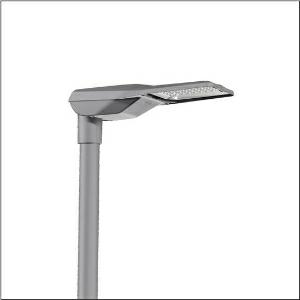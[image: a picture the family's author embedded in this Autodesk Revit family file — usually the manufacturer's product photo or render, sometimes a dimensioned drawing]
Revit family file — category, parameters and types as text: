
# Revit family: streetlight_sl_21_iq_mini___st1_0a_5xe2d31g08gb_f91a
name_source: partatom
category: Lighting Fixtures
units: mm (PartAtom-declared; Revit-internal decimal feet)

## family parameters
Cut with Voids When Loaded = No
Host = Face
Light Source = No
Part Type = Normal
Room Calculation Point = No
Round Connector Dimension = Use Diameter
Shared = No

## types (1)
- --- (1 x LED, 5680 lm, 37.1 W, 3000K)
    Apparent Load = 37 VA
    CIE Flux Codes = 37 72 97 100 100
    Color Rendering = 70
    Color Temperature = 3000K
    Default Elevation = 1800 mm
    Description = Streetlight SL 21 iQ mini, mast luminaire, primary light control with lens, of PMMA, primary optical cover: cover, of toughened safety glass, transparent, light distribution: ST1.0a, light emission: direct distribution, primary light characteristic: asymmetric, installation type: post-top, side-entry, LED, High Power LED, rated luminous flux: 5.680lm, luminous efficacy: 153lm/W, light colour: 730, colour temperature: 3000K, control gear: iQ Street-Remote, control: Street-Remote, Auto-Match, Temp-Guard, Lumen-Switch, Night-Set, Smart-Wire, Light-Fading, Desk-Remote (wireless, voltage-free reading and setting of iQ features in the workshop via application-optimized NFC function/RFID function), optimised constant luminous flux control (CLO 2.0), pre-setting: linear dimming characteristic, mains connection: 220..240V, AC, 50/60Hz, start of lifetime: 37W, end of service life: 39W, reduction: 18W, luminaire housing, of diecast aluminium, powder-coated, Siteco® metallic grey (DB 702S), corrosivity category C5 mid according to DIN EN ISO 12944, please order mast flange separately, inclination adjustable: 0°, 5°, 10°, 15°, sealing non-destructively replaceable, multi-level sealing system, length: 628mm, width: 235mm, height: 110mm, mast flange for spigot size: 42mm (side-entry): 5XC10008XM4, 60/48mm (side-entry/post-top): 5XC10108XM2, 76/60mm (side-entry/post-top): 5XC10108XM1, mounting height: 4..8m, protection rating (complete): IP66, insulation class (complete): insulation class II (safety insulation), certification: CE, ENEC, ENEC+, VDE, impact resistance: IK10, permissible operating ambient temperature for outdoor applications: -40..+50°C, standard-compliant lighting for roads and squares, packaging unit: 1 piece

Light Distribution: ST1.0a
    Height = 110 mm
    Lamp = 1 x LED
    Lamp Light Flux = 5680 lm
    Lamp Power = 37.1 W
    Lamp count = 1
    Length = 625 mm
    Luminous efficacy = 153 lm/W
    Manufacturer = Siteco
    ModVariant = No
    Model = 5XE2D31G08GB
    Number of Poles = 1
    OnlyDefault = Yes
    Power Factor = 1
    Product Name = Streetlight SL 21 iQ mini | ST1.0a
    Product group = mast luminaire | pylon top
    ProductGroupID = 6100
    Protection Class = Protection class II
    Protection Degree = IP 66
    RLX_Detail_Level = 1
    RLX_Emergency_Light_Flux = 0 lm
    RLX_Emergency_Type = 0
    RLX_Emergency_Type_DB = No
    RlxData = <blob elided: 26361 chars, md5=81ec1625>
    Socket = socket
    Standby Power = 0 W
    System Light Flux = 5680 lm
    System Power = 37 W
    Type Comments = factory setting: luminous flux: 100 % | dim-lin: 254 | 385 mA
    Type Image = l_1003519.jpg
    URL = http://relux.com
    VarID = @adj_210217
    Voltage = 0 V
    Weight = 0.00 kg
    Width = 234 mm

## geometry (parser evidence)
native form markers: Blend x4, Sweep x11
no freeform markers — native parametric forms only
